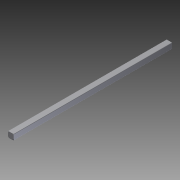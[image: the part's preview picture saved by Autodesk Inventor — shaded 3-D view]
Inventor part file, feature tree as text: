
AUTODESK INVENTOR PART (.ipt)
format: ipt  version: 2012 (Build 160160000, 160)  size: 118,784 bytes
history: native  units: in
note: dims shown in document units (in); Inventor stores cm internally (conversion verified against a paired STEP export)
features: other x1, imported_body x1, plane x1, split x1
ambient origin geometry x8: Origin, YZ Plane, XZ Plane, XY Plane, X Axis, Y Axis, Z Axis, Center Point
feature tree (4):
  parser-record x1  (decoder bookkeeping rows leaked as tree rows — omitted from the tree; the rows remain in map.json)
  imported_body  "Base1"
  plane  "Work Plane1"
  split  "Split1"
